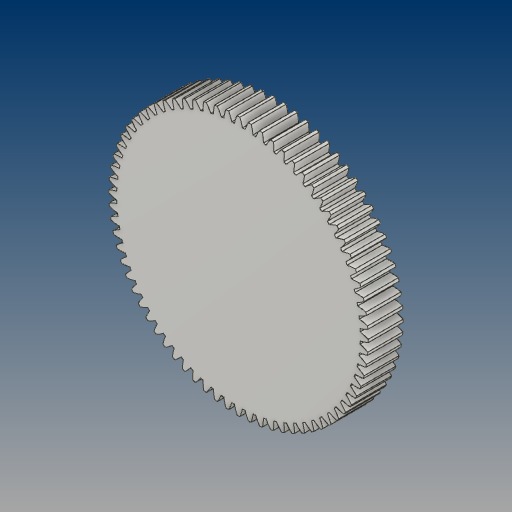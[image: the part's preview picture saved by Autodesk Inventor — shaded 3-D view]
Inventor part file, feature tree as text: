
AUTODESK INVENTOR PART (.ipt)
format: ipt  version: 2021 (Build 250183000, 183)  size: 447,488 bytes
history: native  units: mm (DEFAULTED — no unit token found)
features: plane x3, other x3, sketch x2, extrude x1
ambient origin geometry x8: Origin, YZ Plane, XZ Plane, XY Plane, X Axis, Y Axis, Z Axis, Center Point
bodies: Solid1 (feature_tree)
feature tree (9):
  extrude  "Extrusion1"  Depth=20.0mm TaperAngle=0.0deg
  plane  "Work Plane2"
  plane  "Work Plane8"
  plane  "Work Plane9"
  other  "Spur Gear"
  sketch  "Sketch1"  dims[d0=148.0mm d1=20.0mm d2=0.0mm]
  sketch  "Sketch2"  dims[d3=144.0mm d4=10.0mm d5=0.0mm d16=90.0mm d17=0.0mm d34=0.436332mm d39=0.0mm d41=0.0mm d43=90.0mm d46=90.0mm d47=0.0mm d48=0.0mm]
  other  "Srf1"
  other  "Pitch Diameter"
